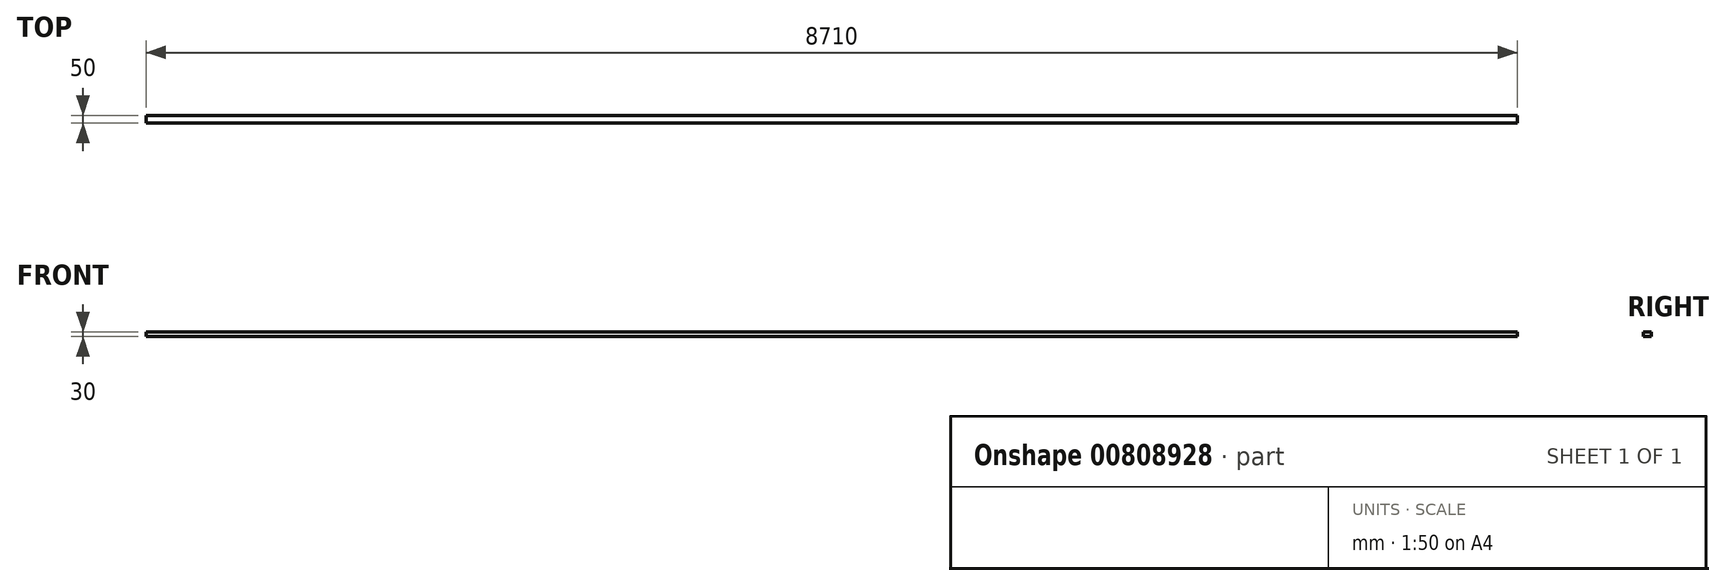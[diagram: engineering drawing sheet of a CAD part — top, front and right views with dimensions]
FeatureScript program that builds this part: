
annotation { "Feature Type Name" : "Feature", "Feature Type Description" : "" }
export const myFeature = defineFeature(function(context is Context, id is Id, definition is map)
    precondition{}
    {
        {
            var Q0;
            Q0=qCreatedBy(makeId("Right.planeOp"),FACE);
            var sketch = newSketch(context, id + "F0", { "sketchPlane" : qUnion([Q0])});
            skLineSegment(sketch, "E0.bottom", {"start": v(0, 0) * mm, "end": v(-50, 0) * mm});
            skLineSegment(sketch, "E0.top", {"start": v(0, 30) * mm, "end": v(-50, 30) * mm});
            skLineSegment(sketch, "E0.left", {"start": v(0, 0) * mm, "end": v(0, 30) * mm});
            skLineSegment(sketch, "E0.right", {"start": v(-50, 0) * mm, "end": v(-50, 30) * mm});
            skSolve(sketch);
        }
        {
            var Q0;
            Q0 = qSketchRegion(id + "F0", true);
            extrude(context, id + "F1", {"entities" : qUnion([Q0]), "depth" : 8710 * mm, "offsetDistance" : 25 * mm});
        }
    });
